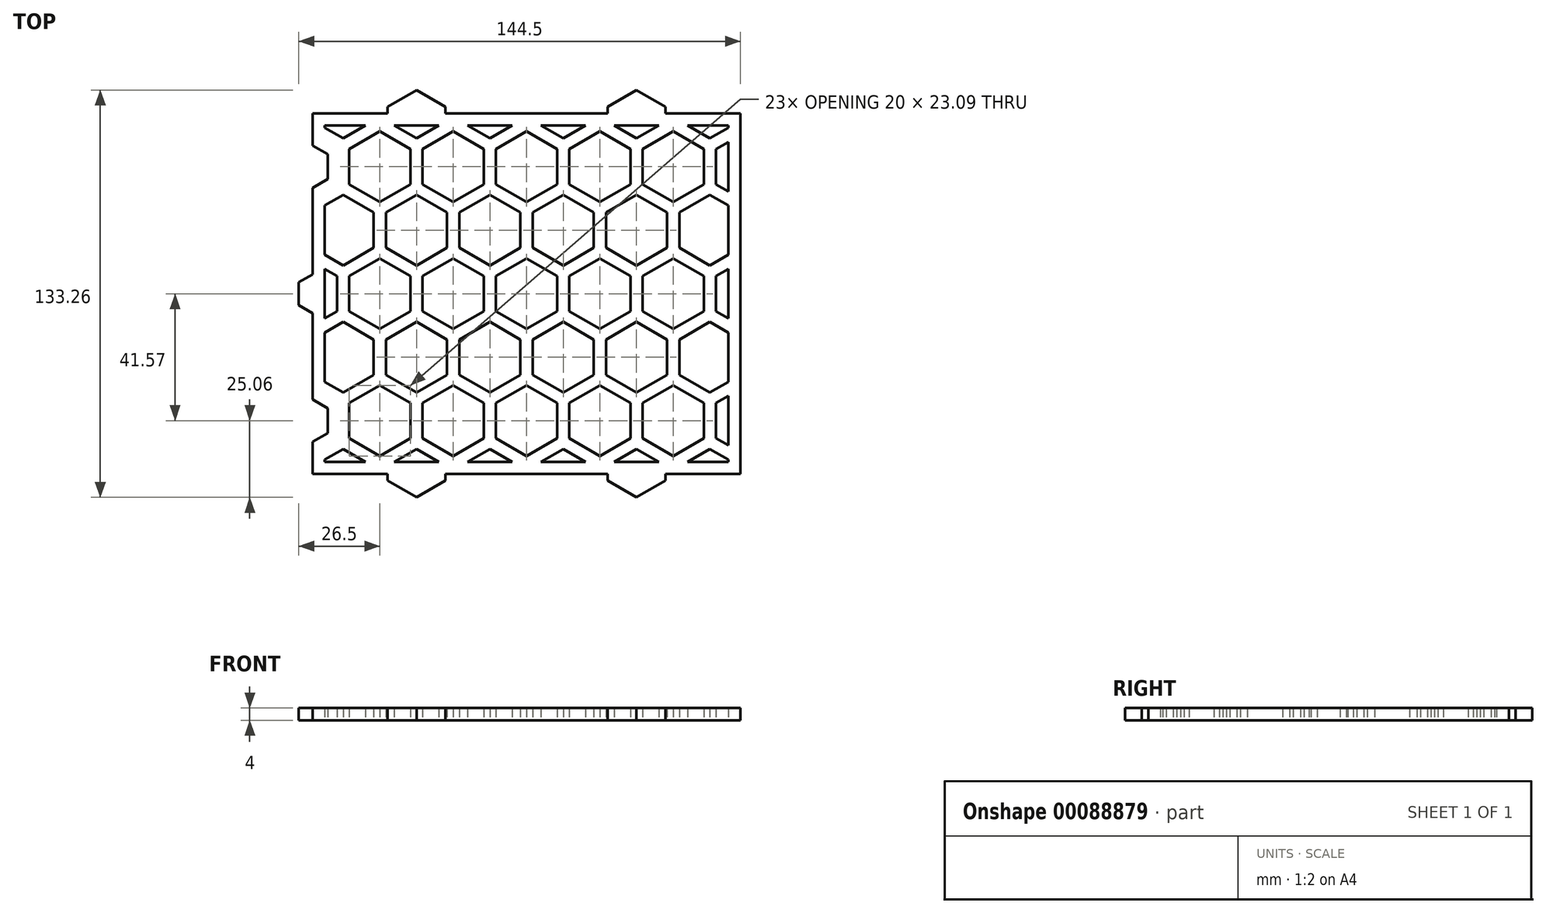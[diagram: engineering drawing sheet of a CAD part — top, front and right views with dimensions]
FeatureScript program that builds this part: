
annotation { "Feature Type Name" : "Feature", "Feature Type Description" : "" }
export const myFeature = defineFeature(function(context is Context, id is Id, definition is map)
    precondition{}
    {
        {
            var Q0;
            Q0=qCreatedBy(makeId("Top.planeOp"),FACE);
            var sketch = newSketch(context, id + "F0", { "sketchPlane" : qUnion([Q0])});
            skLineSegment(sketch, "E0.bottom", {"start": v(70, -59) * mm, "end": v(-70, -59) * mm});
            skLineSegment(sketch, "E0.top", {"start": v(70, 59) * mm, "end": v(-70, 59) * mm});
            skLineSegment(sketch, "E0.left", {"start": v(70, -59) * mm, "end": v(70, 59) * mm});
            skLineSegment(sketch, "E0.right", {"start": v(-70, -59) * mm, "end": v(-70, 59) * mm});
            skPoint(sketch, "E0.middle", {"position": v(0, 0) * mm});
            skLineSegment(sketch, "E1.0", {"start": v(-66, -55) * mm, "end": v(-66, 55) * mm});
            skLineSegment(sketch, "E1.1", {"start": v(66, -55) * mm, "end": v(-66, -55) * mm});
            skLineSegment(sketch, "E1.2", {"start": v(66, -55) * mm, "end": v(66, 55) * mm});
            skLineSegment(sketch, "E1.3", {"start": v(66, 55) * mm, "end": v(-66, 55) * mm});
            skSolve(sketch);
        }
        {
            var Q0;
            Q0=qSketchRegion(id+"F0",true);
            extrude(context, id + "F1", {"entities" : qUnion([Q0]), "depth" : 4 * mm});
        }
        {
            var Q0;
            Q0=qCreatedBy(makeId("Top.planeOp"),FACE);
            var sketch = newSketch(context, id + "F2", { "sketchPlane" : qUnion([Q0])});
            skLineSegment(sketch, "E2.0.1.1", {"start": v(-62, -47.34) * mm, "end": v(-66, -49.65) * mm});
            skLineSegment(sketch, "E2.0.1.5", {"start": v(-66, -33.49) * mm, "end": v(-62, -35.8) * mm});
            skLineSegment(sketch, "E2.0.1.13", {"start": v(-62, -35.8) * mm, "end": v(-62, -47.34) * mm});
            skLineSegment(sketch, "E2.0.2.1", {"start": v(-62, -5.77) * mm, "end": v(-66, -8.08) * mm});
            skLineSegment(sketch, "E2.0.2.5", {"start": v(-66, 8.08) * mm, "end": v(-62, 5.77) * mm});
            skLineSegment(sketch, "E2.0.2.13", {"start": v(-62, 5.77) * mm, "end": v(-62, -5.77) * mm});
            skLineSegment(sketch, "E2.0.3.1", {"start": v(-62, 35.8) * mm, "end": v(-66, 33.49) * mm});
            skLineSegment(sketch, "E2.0.3.5", {"start": v(-66, 49.65) * mm, "end": v(-62, 47.34) * mm});
            skLineSegment(sketch, "E2.0.3.13", {"start": v(-62, 47.34) * mm, "end": v(-62, 35.8) * mm});
            skLineSegment(sketch, "E2.1.0.7", {"start": v(-60, -50.8) * mm, "end": v(-52.74, -55) * mm});
            skLineSegment(sketch, "E2.1.0.8", {"start": v(-66, -54.27) * mm, "end": v(-60, -50.8) * mm});
            skCircle(sketch, "E2.1.1.0", {"center": v(-48, -41.57) * mm, "radius": 11.55 * mm, "construction": true});
            skLineSegment(sketch, "E2.1.1.1", {"start": v(-38, -47.34) * mm, "end": v(-48, -53.12) * mm});
            skLineSegment(sketch, "E2.1.1.2", {"start": v(-48, -53.12) * mm, "end": v(-58, -47.34) * mm});
            skLineSegment(sketch, "E2.1.1.3", {"start": v(-58, -47.34) * mm, "end": v(-58, -35.8) * mm});
            skLineSegment(sketch, "E2.1.1.4", {"start": v(-58, -35.8) * mm, "end": v(-48, -30.02) * mm});
            skLineSegment(sketch, "E2.1.1.5", {"start": v(-48, -30.02) * mm, "end": v(-38, -35.8) * mm});
            skLineSegment(sketch, "E2.1.1.6", {"start": v(-50, -15.01) * mm, "end": v(-50, -26.56) * mm});
            skLineSegment(sketch, "E2.1.1.7", {"start": v(-60, -9.24) * mm, "end": v(-50, -15.01) * mm});
            skLineSegment(sketch, "E2.1.1.8", {"start": v(-66, -12.7) * mm, "end": v(-60, -9.24) * mm});
            skLineSegment(sketch, "E2.1.1.10", {"start": v(-60, -32.33) * mm, "end": v(-66, -28.87) * mm});
            skLineSegment(sketch, "E2.1.1.11", {"start": v(-50, -26.56) * mm, "end": v(-60, -32.33) * mm});
            skLineSegment(sketch, "E2.1.1.13", {"start": v(-38, -35.8) * mm, "end": v(-38, -47.34) * mm});
            skCircle(sketch, "E2.1.2.0", {"center": v(-48, 0) * mm, "radius": 11.55 * mm, "construction": true});
            skLineSegment(sketch, "E2.1.2.1", {"start": v(-38, -5.77) * mm, "end": v(-48, -11.55) * mm});
            skLineSegment(sketch, "E2.1.2.2", {"start": v(-48, -11.55) * mm, "end": v(-58, -5.77) * mm});
            skLineSegment(sketch, "E2.1.2.3", {"start": v(-58, -5.77) * mm, "end": v(-58, 5.77) * mm});
            skLineSegment(sketch, "E2.1.2.4", {"start": v(-58, 5.77) * mm, "end": v(-48, 11.55) * mm});
            skLineSegment(sketch, "E2.1.2.5", {"start": v(-48, 11.55) * mm, "end": v(-38, 5.77) * mm});
            skLineSegment(sketch, "E2.1.2.6", {"start": v(-50, 26.56) * mm, "end": v(-50, 15.01) * mm});
            skLineSegment(sketch, "E2.1.2.7", {"start": v(-60, 32.33) * mm, "end": v(-50, 26.56) * mm});
            skLineSegment(sketch, "E2.1.2.8", {"start": v(-66, 28.87) * mm, "end": v(-60, 32.33) * mm});
            skLineSegment(sketch, "E2.1.2.10", {"start": v(-60, 9.24) * mm, "end": v(-66, 12.7) * mm});
            skLineSegment(sketch, "E2.1.2.11", {"start": v(-50, 15.01) * mm, "end": v(-60, 9.24) * mm});
            skLineSegment(sketch, "E2.1.2.13", {"start": v(-38, 5.77) * mm, "end": v(-38, -5.77) * mm});
            skCircle(sketch, "E2.1.3.0", {"center": v(-48, 41.57) * mm, "radius": 11.55 * mm, "construction": true});
            skLineSegment(sketch, "E2.1.3.1", {"start": v(-38, 35.8) * mm, "end": v(-48, 30.02) * mm});
            skLineSegment(sketch, "E2.1.3.2", {"start": v(-48, 30.02) * mm, "end": v(-58, 35.8) * mm});
            skLineSegment(sketch, "E2.1.3.3", {"start": v(-58, 35.8) * mm, "end": v(-58, 47.34) * mm});
            skLineSegment(sketch, "E2.1.3.4", {"start": v(-58, 47.34) * mm, "end": v(-48, 53.12) * mm});
            skLineSegment(sketch, "E2.1.3.5", {"start": v(-48, 53.12) * mm, "end": v(-38, 47.34) * mm});
            skLineSegment(sketch, "E2.1.3.10", {"start": v(-60, 50.8) * mm, "end": v(-66, 54.27) * mm});
            skLineSegment(sketch, "E2.1.3.11", {"start": v(-52.74, 55) * mm, "end": v(-60, 50.8) * mm});
            skLineSegment(sketch, "E2.1.3.13", {"start": v(-38, 47.34) * mm, "end": v(-38, 35.8) * mm});
            skLineSegment(sketch, "E2.2.0.7", {"start": v(-36, -50.8) * mm, "end": v(-28.74, -55) * mm});
            skLineSegment(sketch, "E2.2.0.8", {"start": v(-43.26, -55) * mm, "end": v(-36, -50.8) * mm});
            skCircle(sketch, "E2.2.1.0", {"center": v(-24, -41.57) * mm, "radius": 11.55 * mm, "construction": true});
            skLineSegment(sketch, "E2.2.1.1", {"start": v(-14, -47.34) * mm, "end": v(-24, -53.12) * mm});
            skLineSegment(sketch, "E2.2.1.2", {"start": v(-24, -53.12) * mm, "end": v(-34, -47.34) * mm});
            skLineSegment(sketch, "E2.2.1.3", {"start": v(-34, -47.34) * mm, "end": v(-34, -35.8) * mm});
            skLineSegment(sketch, "E2.2.1.4", {"start": v(-34, -35.8) * mm, "end": v(-24, -30.02) * mm});
            skLineSegment(sketch, "E2.2.1.5", {"start": v(-24, -30.02) * mm, "end": v(-14, -35.8) * mm});
            skLineSegment(sketch, "E2.2.1.6", {"start": v(-26, -15.01) * mm, "end": v(-26, -26.56) * mm});
            skLineSegment(sketch, "E2.2.1.7", {"start": v(-36, -9.24) * mm, "end": v(-26, -15.01) * mm});
            skLineSegment(sketch, "E2.2.1.8", {"start": v(-46, -15.01) * mm, "end": v(-36, -9.24) * mm});
            skLineSegment(sketch, "E2.2.1.9", {"start": v(-46, -26.56) * mm, "end": v(-46, -15.01) * mm});
            skLineSegment(sketch, "E2.2.1.10", {"start": v(-36, -32.33) * mm, "end": v(-46, -26.56) * mm});
            skLineSegment(sketch, "E2.2.1.11", {"start": v(-26, -26.56) * mm, "end": v(-36, -32.33) * mm});
            skCircle(sketch, "E2.2.1.12", {"center": v(-36, -20.79) * mm, "radius": 11.55 * mm, "construction": true});
            skLineSegment(sketch, "E2.2.1.13", {"start": v(-14, -35.8) * mm, "end": v(-14, -47.34) * mm});
            skCircle(sketch, "E2.2.2.0", {"center": v(-24, 0) * mm, "radius": 11.55 * mm, "construction": true});
            skLineSegment(sketch, "E2.2.2.1", {"start": v(-14, -5.77) * mm, "end": v(-24, -11.55) * mm});
            skLineSegment(sketch, "E2.2.2.2", {"start": v(-24, -11.55) * mm, "end": v(-34, -5.77) * mm});
            skLineSegment(sketch, "E2.2.2.3", {"start": v(-34, -5.77) * mm, "end": v(-34, 5.77) * mm});
            skLineSegment(sketch, "E2.2.2.4", {"start": v(-34, 5.77) * mm, "end": v(-24, 11.55) * mm});
            skLineSegment(sketch, "E2.2.2.5", {"start": v(-24, 11.55) * mm, "end": v(-14, 5.77) * mm});
            skLineSegment(sketch, "E2.2.2.6", {"start": v(-26, 26.56) * mm, "end": v(-26, 15.01) * mm});
            skLineSegment(sketch, "E2.2.2.7", {"start": v(-36, 32.33) * mm, "end": v(-26, 26.56) * mm});
            skLineSegment(sketch, "E2.2.2.8", {"start": v(-46, 26.56) * mm, "end": v(-36, 32.33) * mm});
            skLineSegment(sketch, "E2.2.2.9", {"start": v(-46, 15.01) * mm, "end": v(-46, 26.56) * mm});
            skLineSegment(sketch, "E2.2.2.10", {"start": v(-36, 9.24) * mm, "end": v(-46, 15.01) * mm});
            skLineSegment(sketch, "E2.2.2.11", {"start": v(-26, 15.01) * mm, "end": v(-36, 9.24) * mm});
            skCircle(sketch, "E2.2.2.12", {"center": v(-36, 20.78) * mm, "radius": 11.55 * mm, "construction": true});
            skLineSegment(sketch, "E2.2.2.13", {"start": v(-14, 5.77) * mm, "end": v(-14, -5.77) * mm});
            skCircle(sketch, "E2.2.3.0", {"center": v(-24, 41.57) * mm, "radius": 11.55 * mm, "construction": true});
            skLineSegment(sketch, "E2.2.3.1", {"start": v(-14, 35.8) * mm, "end": v(-24, 30.02) * mm});
            skLineSegment(sketch, "E2.2.3.2", {"start": v(-24, 30.02) * mm, "end": v(-34, 35.8) * mm});
            skLineSegment(sketch, "E2.2.3.3", {"start": v(-34, 35.8) * mm, "end": v(-34, 47.34) * mm});
            skLineSegment(sketch, "E2.2.3.4", {"start": v(-34, 47.34) * mm, "end": v(-24, 53.12) * mm});
            skLineSegment(sketch, "E2.2.3.5", {"start": v(-24, 53.12) * mm, "end": v(-14, 47.34) * mm});
            skLineSegment(sketch, "E2.2.3.10", {"start": v(-36, 50.8) * mm, "end": v(-43.26, 55) * mm});
            skLineSegment(sketch, "E2.2.3.11", {"start": v(-28.74, 55) * mm, "end": v(-36, 50.8) * mm});
            skLineSegment(sketch, "E2.2.3.13", {"start": v(-14, 47.34) * mm, "end": v(-14, 35.8) * mm});
            skLineSegment(sketch, "E2.3.0.7", {"start": v(-12, -50.8) * mm, "end": v(-4.74, -55) * mm});
            skLineSegment(sketch, "E2.3.0.8", {"start": v(-19.26, -55) * mm, "end": v(-12, -50.8) * mm});
            skCircle(sketch, "E2.3.1.0", {"center": v(0, -41.57) * mm, "radius": 11.55 * mm, "construction": true});
            skLineSegment(sketch, "E2.3.1.1", {"start": v(10, -47.34) * mm, "end": v(0, -53.12) * mm});
            skLineSegment(sketch, "E2.3.1.2", {"start": v(0, -53.12) * mm, "end": v(-10, -47.34) * mm});
            skLineSegment(sketch, "E2.3.1.3", {"start": v(-10, -47.34) * mm, "end": v(-10, -35.8) * mm});
            skLineSegment(sketch, "E2.3.1.4", {"start": v(-10, -35.8) * mm, "end": v(0, -30.02) * mm});
            skLineSegment(sketch, "E2.3.1.5", {"start": v(0, -30.02) * mm, "end": v(10, -35.8) * mm});
            skLineSegment(sketch, "E2.3.1.6", {"start": v(-2, -15.01) * mm, "end": v(-2, -26.56) * mm});
            skLineSegment(sketch, "E2.3.1.7", {"start": v(-12, -9.24) * mm, "end": v(-2, -15.01) * mm});
            skLineSegment(sketch, "E2.3.1.8", {"start": v(-22, -15.01) * mm, "end": v(-12, -9.24) * mm});
            skLineSegment(sketch, "E2.3.1.9", {"start": v(-22, -26.56) * mm, "end": v(-22, -15.01) * mm});
            skLineSegment(sketch, "E2.3.1.10", {"start": v(-12, -32.33) * mm, "end": v(-22, -26.56) * mm});
            skLineSegment(sketch, "E2.3.1.11", {"start": v(-2, -26.56) * mm, "end": v(-12, -32.33) * mm});
            skCircle(sketch, "E2.3.1.12", {"center": v(-12, -20.79) * mm, "radius": 11.55 * mm, "construction": true});
            skLineSegment(sketch, "E2.3.1.13", {"start": v(10, -35.8) * mm, "end": v(10, -47.34) * mm});
            skCircle(sketch, "E2.3.2.0", {"center": v(0, 0) * mm, "radius": 11.55 * mm, "construction": true});
            skLineSegment(sketch, "E2.3.2.1", {"start": v(10, -5.77) * mm, "end": v(0, -11.55) * mm});
            skLineSegment(sketch, "E2.3.2.2", {"start": v(0, -11.55) * mm, "end": v(-10, -5.77) * mm});
            skLineSegment(sketch, "E2.3.2.3", {"start": v(-10, -5.77) * mm, "end": v(-10, 5.77) * mm});
            skLineSegment(sketch, "E2.3.2.4", {"start": v(-10, 5.77) * mm, "end": v(0, 11.55) * mm});
            skLineSegment(sketch, "E2.3.2.5", {"start": v(0, 11.55) * mm, "end": v(10, 5.77) * mm});
            skLineSegment(sketch, "E2.3.2.6", {"start": v(-2, 26.56) * mm, "end": v(-2, 15.01) * mm});
            skLineSegment(sketch, "E2.3.2.7", {"start": v(-12, 32.33) * mm, "end": v(-2, 26.56) * mm});
            skLineSegment(sketch, "E2.3.2.8", {"start": v(-22, 26.56) * mm, "end": v(-12, 32.33) * mm});
            skLineSegment(sketch, "E2.3.2.9", {"start": v(-22, 15.01) * mm, "end": v(-22, 26.56) * mm});
            skLineSegment(sketch, "E2.3.2.10", {"start": v(-12, 9.24) * mm, "end": v(-22, 15.01) * mm});
            skLineSegment(sketch, "E2.3.2.11", {"start": v(-2, 15.01) * mm, "end": v(-12, 9.24) * mm});
            skCircle(sketch, "E2.3.2.12", {"center": v(-12, 20.78) * mm, "radius": 11.55 * mm, "construction": true});
            skLineSegment(sketch, "E2.3.2.13", {"start": v(10, 5.77) * mm, "end": v(10, -5.77) * mm});
            skCircle(sketch, "E2.3.3.0", {"center": v(0, 41.57) * mm, "radius": 11.55 * mm, "construction": true});
            skLineSegment(sketch, "E2.3.3.1", {"start": v(10, 35.8) * mm, "end": v(0, 30.02) * mm});
            skLineSegment(sketch, "E2.3.3.2", {"start": v(0, 30.02) * mm, "end": v(-10, 35.8) * mm});
            skLineSegment(sketch, "E2.3.3.3", {"start": v(-10, 35.8) * mm, "end": v(-10, 47.34) * mm});
            skLineSegment(sketch, "E2.3.3.4", {"start": v(-10, 47.34) * mm, "end": v(0, 53.12) * mm});
            skLineSegment(sketch, "E2.3.3.5", {"start": v(0, 53.12) * mm, "end": v(10, 47.34) * mm});
            skLineSegment(sketch, "E2.3.3.10", {"start": v(-12, 50.8) * mm, "end": v(-19.26, 55) * mm});
            skLineSegment(sketch, "E2.3.3.11", {"start": v(-4.74, 55) * mm, "end": v(-12, 50.8) * mm});
            skLineSegment(sketch, "E2.3.3.13", {"start": v(10, 47.34) * mm, "end": v(10, 35.8) * mm});
            skLineSegment(sketch, "E2.4.0.7", {"start": v(12, -50.8) * mm, "end": v(19.26, -55) * mm});
            skLineSegment(sketch, "E2.4.0.8", {"start": v(4.74, -55) * mm, "end": v(12, -50.8) * mm});
            skCircle(sketch, "E2.4.1.0", {"center": v(24, -41.57) * mm, "radius": 11.55 * mm, "construction": true});
            skLineSegment(sketch, "E2.4.1.1", {"start": v(34, -47.34) * mm, "end": v(24, -53.12) * mm});
            skLineSegment(sketch, "E2.4.1.2", {"start": v(24, -53.12) * mm, "end": v(14, -47.34) * mm});
            skLineSegment(sketch, "E2.4.1.3", {"start": v(14, -47.34) * mm, "end": v(14, -35.8) * mm});
            skLineSegment(sketch, "E2.4.1.4", {"start": v(14, -35.8) * mm, "end": v(24, -30.02) * mm});
            skLineSegment(sketch, "E2.4.1.5", {"start": v(24, -30.02) * mm, "end": v(34, -35.8) * mm});
            skLineSegment(sketch, "E2.4.1.6", {"start": v(22, -15.01) * mm, "end": v(22, -26.56) * mm});
            skLineSegment(sketch, "E2.4.1.7", {"start": v(12, -9.24) * mm, "end": v(22, -15.01) * mm});
            skLineSegment(sketch, "E2.4.1.8", {"start": v(2, -15.01) * mm, "end": v(12, -9.24) * mm});
            skLineSegment(sketch, "E2.4.1.9", {"start": v(2, -26.56) * mm, "end": v(2, -15.01) * mm});
            skLineSegment(sketch, "E2.4.1.10", {"start": v(12, -32.33) * mm, "end": v(2, -26.56) * mm});
            skLineSegment(sketch, "E2.4.1.11", {"start": v(22, -26.56) * mm, "end": v(12, -32.33) * mm});
            skCircle(sketch, "E2.4.1.12", {"center": v(12, -20.79) * mm, "radius": 11.55 * mm, "construction": true});
            skLineSegment(sketch, "E2.4.1.13", {"start": v(34, -35.8) * mm, "end": v(34, -47.34) * mm});
            skCircle(sketch, "E2.4.2.0", {"center": v(24, 0) * mm, "radius": 11.55 * mm, "construction": true});
            skLineSegment(sketch, "E2.4.2.1", {"start": v(34, -5.77) * mm, "end": v(24, -11.55) * mm});
            skLineSegment(sketch, "E2.4.2.2", {"start": v(24, -11.55) * mm, "end": v(14, -5.77) * mm});
            skLineSegment(sketch, "E2.4.2.3", {"start": v(14, -5.77) * mm, "end": v(14, 5.77) * mm});
            skLineSegment(sketch, "E2.4.2.4", {"start": v(14, 5.77) * mm, "end": v(24, 11.55) * mm});
            skLineSegment(sketch, "E2.4.2.5", {"start": v(24, 11.55) * mm, "end": v(34, 5.77) * mm});
            skLineSegment(sketch, "E2.4.2.6", {"start": v(22, 26.56) * mm, "end": v(22, 15.01) * mm});
            skLineSegment(sketch, "E2.4.2.7", {"start": v(12, 32.33) * mm, "end": v(22, 26.56) * mm});
            skLineSegment(sketch, "E2.4.2.8", {"start": v(2, 26.56) * mm, "end": v(12, 32.33) * mm});
            skLineSegment(sketch, "E2.4.2.9", {"start": v(2, 15.01) * mm, "end": v(2, 26.56) * mm});
            skLineSegment(sketch, "E2.4.2.10", {"start": v(12, 9.24) * mm, "end": v(2, 15.01) * mm});
            skLineSegment(sketch, "E2.4.2.11", {"start": v(22, 15.01) * mm, "end": v(12, 9.24) * mm});
            skCircle(sketch, "E2.4.2.12", {"center": v(12, 20.78) * mm, "radius": 11.55 * mm, "construction": true});
            skLineSegment(sketch, "E2.4.2.13", {"start": v(34, 5.77) * mm, "end": v(34, -5.77) * mm});
            skCircle(sketch, "E2.4.3.0", {"center": v(24, 41.57) * mm, "radius": 11.55 * mm, "construction": true});
            skLineSegment(sketch, "E2.4.3.1", {"start": v(34, 35.8) * mm, "end": v(24, 30.02) * mm});
            skLineSegment(sketch, "E2.4.3.2", {"start": v(24, 30.02) * mm, "end": v(14, 35.8) * mm});
            skLineSegment(sketch, "E2.4.3.3", {"start": v(14, 35.8) * mm, "end": v(14, 47.34) * mm});
            skLineSegment(sketch, "E2.4.3.4", {"start": v(14, 47.34) * mm, "end": v(24, 53.12) * mm});
            skLineSegment(sketch, "E2.4.3.5", {"start": v(24, 53.12) * mm, "end": v(34, 47.34) * mm});
            skLineSegment(sketch, "E2.4.3.10", {"start": v(12, 50.8) * mm, "end": v(4.74, 55) * mm});
            skLineSegment(sketch, "E2.4.3.11", {"start": v(19.26, 55) * mm, "end": v(12, 50.8) * mm});
            skLineSegment(sketch, "E2.4.3.13", {"start": v(34, 47.34) * mm, "end": v(34, 35.8) * mm});
            skLineSegment(sketch, "E2.5.0.7", {"start": v(36, -50.8) * mm, "end": v(43.26, -55) * mm});
            skLineSegment(sketch, "E2.5.0.8", {"start": v(28.74, -55) * mm, "end": v(36, -50.8) * mm});
            skCircle(sketch, "E2.5.1.0", {"center": v(48, -41.57) * mm, "radius": 11.55 * mm, "construction": true});
            skLineSegment(sketch, "E2.5.1.1", {"start": v(58, -47.34) * mm, "end": v(48, -53.12) * mm});
            skLineSegment(sketch, "E2.5.1.2", {"start": v(48, -53.12) * mm, "end": v(38, -47.34) * mm});
            skLineSegment(sketch, "E2.5.1.3", {"start": v(38, -47.34) * mm, "end": v(38, -35.8) * mm});
            skLineSegment(sketch, "E2.5.1.4", {"start": v(38, -35.8) * mm, "end": v(48, -30.02) * mm});
            skLineSegment(sketch, "E2.5.1.5", {"start": v(48, -30.02) * mm, "end": v(58, -35.8) * mm});
            skLineSegment(sketch, "E2.5.1.6", {"start": v(46, -15.01) * mm, "end": v(46, -26.56) * mm});
            skLineSegment(sketch, "E2.5.1.7", {"start": v(36, -9.24) * mm, "end": v(46, -15.01) * mm});
            skLineSegment(sketch, "E2.5.1.8", {"start": v(26, -15.01) * mm, "end": v(36, -9.24) * mm});
            skLineSegment(sketch, "E2.5.1.9", {"start": v(26, -26.56) * mm, "end": v(26, -15.01) * mm});
            skLineSegment(sketch, "E2.5.1.10", {"start": v(36, -32.33) * mm, "end": v(26, -26.56) * mm});
            skLineSegment(sketch, "E2.5.1.11", {"start": v(46, -26.56) * mm, "end": v(36, -32.33) * mm});
            skCircle(sketch, "E2.5.1.12", {"center": v(36, -20.79) * mm, "radius": 11.55 * mm, "construction": true});
            skLineSegment(sketch, "E2.5.1.13", {"start": v(58, -35.8) * mm, "end": v(58, -47.34) * mm});
            skCircle(sketch, "E2.5.2.0", {"center": v(48, 0) * mm, "radius": 11.55 * mm, "construction": true});
            skLineSegment(sketch, "E2.5.2.1", {"start": v(58, -5.77) * mm, "end": v(48, -11.55) * mm});
            skLineSegment(sketch, "E2.5.2.2", {"start": v(48, -11.55) * mm, "end": v(38, -5.77) * mm});
            skLineSegment(sketch, "E2.5.2.3", {"start": v(38, -5.77) * mm, "end": v(38, 5.77) * mm});
            skLineSegment(sketch, "E2.5.2.4", {"start": v(38, 5.77) * mm, "end": v(48, 11.55) * mm});
            skLineSegment(sketch, "E2.5.2.5", {"start": v(48, 11.55) * mm, "end": v(58, 5.77) * mm});
            skLineSegment(sketch, "E2.5.2.6", {"start": v(46, 26.56) * mm, "end": v(46, 15.01) * mm});
            skLineSegment(sketch, "E2.5.2.7", {"start": v(36, 32.33) * mm, "end": v(46, 26.56) * mm});
            skLineSegment(sketch, "E2.5.2.8", {"start": v(26, 26.56) * mm, "end": v(36, 32.33) * mm});
            skLineSegment(sketch, "E2.5.2.9", {"start": v(26, 15.01) * mm, "end": v(26, 26.56) * mm});
            skLineSegment(sketch, "E2.5.2.10", {"start": v(36, 9.24) * mm, "end": v(26, 15.01) * mm});
            skLineSegment(sketch, "E2.5.2.11", {"start": v(46, 15.01) * mm, "end": v(36, 9.24) * mm});
            skCircle(sketch, "E2.5.2.12", {"center": v(36, 20.78) * mm, "radius": 11.55 * mm, "construction": true});
            skLineSegment(sketch, "E2.5.2.13", {"start": v(58, 5.77) * mm, "end": v(58, -5.77) * mm});
            skCircle(sketch, "E2.5.3.0", {"center": v(48, 41.57) * mm, "radius": 11.55 * mm, "construction": true});
            skLineSegment(sketch, "E2.5.3.1", {"start": v(58, 35.8) * mm, "end": v(48, 30.02) * mm});
            skLineSegment(sketch, "E2.5.3.2", {"start": v(48, 30.02) * mm, "end": v(38, 35.8) * mm});
            skLineSegment(sketch, "E2.5.3.3", {"start": v(38, 35.8) * mm, "end": v(38, 47.34) * mm});
            skLineSegment(sketch, "E2.5.3.4", {"start": v(38, 47.34) * mm, "end": v(48, 53.12) * mm});
            skLineSegment(sketch, "E2.5.3.5", {"start": v(48, 53.12) * mm, "end": v(58, 47.34) * mm});
            skLineSegment(sketch, "E2.5.3.10", {"start": v(36, 50.8) * mm, "end": v(28.74, 55) * mm});
            skLineSegment(sketch, "E2.5.3.11", {"start": v(43.26, 55) * mm, "end": v(36, 50.8) * mm});
            skLineSegment(sketch, "E2.5.3.13", {"start": v(58, 47.34) * mm, "end": v(58, 35.8) * mm});
            skLineSegment(sketch, "E2.6.0.7", {"start": v(60, -50.8) * mm, "end": v(66, -54.27) * mm});
            skLineSegment(sketch, "E2.6.0.8", {"start": v(52.74, -55) * mm, "end": v(60, -50.8) * mm});
            skLineSegment(sketch, "E2.6.1.2", {"start": v(66, -49.65) * mm, "end": v(62, -47.34) * mm});
            skLineSegment(sketch, "E2.6.1.3", {"start": v(62, -47.34) * mm, "end": v(62, -35.8) * mm});
            skLineSegment(sketch, "E2.6.1.4", {"start": v(62, -35.8) * mm, "end": v(66, -33.49) * mm});
            skLineSegment(sketch, "E2.6.1.7", {"start": v(60, -9.24) * mm, "end": v(66, -12.7) * mm});
            skLineSegment(sketch, "E2.6.1.8", {"start": v(50, -15.01) * mm, "end": v(60, -9.24) * mm});
            skLineSegment(sketch, "E2.6.1.9", {"start": v(50, -26.56) * mm, "end": v(50, -15.01) * mm});
            skLineSegment(sketch, "E2.6.1.10", {"start": v(60, -32.33) * mm, "end": v(50, -26.56) * mm});
            skLineSegment(sketch, "E2.6.1.11", {"start": v(66, -28.87) * mm, "end": v(60, -32.33) * mm});
            skLineSegment(sketch, "E2.6.2.2", {"start": v(66, -8.08) * mm, "end": v(62, -5.77) * mm});
            skLineSegment(sketch, "E2.6.2.3", {"start": v(62, -5.77) * mm, "end": v(62, 5.77) * mm});
            skLineSegment(sketch, "E2.6.2.4", {"start": v(62, 5.77) * mm, "end": v(66, 8.08) * mm});
            skLineSegment(sketch, "E2.6.2.7", {"start": v(60, 32.33) * mm, "end": v(66, 28.87) * mm});
            skLineSegment(sketch, "E2.6.2.8", {"start": v(50, 26.56) * mm, "end": v(60, 32.33) * mm});
            skLineSegment(sketch, "E2.6.2.9", {"start": v(50, 15.01) * mm, "end": v(50, 26.56) * mm});
            skLineSegment(sketch, "E2.6.2.10", {"start": v(60, 9.24) * mm, "end": v(50, 15.01) * mm});
            skLineSegment(sketch, "E2.6.2.11", {"start": v(66, 12.7) * mm, "end": v(60, 9.24) * mm});
            skLineSegment(sketch, "E2.6.3.2", {"start": v(66, 33.49) * mm, "end": v(62, 35.8) * mm});
            skLineSegment(sketch, "E2.6.3.3", {"start": v(62, 35.8) * mm, "end": v(62, 47.34) * mm});
            skLineSegment(sketch, "E2.6.3.4", {"start": v(62, 47.34) * mm, "end": v(66, 49.65) * mm});
            skLineSegment(sketch, "E2.6.3.10", {"start": v(60, 50.8) * mm, "end": v(52.74, 55) * mm});
            skLineSegment(sketch, "E2.6.3.11", {"start": v(66, 54.27) * mm, "end": v(60, 50.8) * mm});
            skLineSegment(sketch, "E3.0", {"start": v(-66, -55) * mm, "end": v(-66, -54.27) * mm});
            skLineSegment(sketch, "E3.1", {"start": v(66, 55) * mm, "end": v(52.74, 55) * mm});
            skLineSegment(sketch, "E3.2", {"start": v(66, -55) * mm, "end": v(66, -54.27) * mm});
            skLineSegment(sketch, "E3.3", {"start": v(66, -55) * mm, "end": v(52.74, -55) * mm});
            skLineSegment(sketch, "E4.trimOffspring", {"start": v(-66, 54.27) * mm, "end": v(-66, 55) * mm});
            skLineSegment(sketch, "E5.trimOffspring", {"start": v(-66, 33.49) * mm, "end": v(-66, 49.65) * mm});
            skLineSegment(sketch, "E6.trimOffspring", {"start": v(-66, 12.7) * mm, "end": v(-66, 28.87) * mm});
            skLineSegment(sketch, "E7.trimOffspring", {"start": v(-52.74, 55) * mm, "end": v(-66, 55) * mm});
            skLineSegment(sketch, "E8.trimOffspring", {"start": v(-28.74, 55) * mm, "end": v(-43.26, 55) * mm});
            skLineSegment(sketch, "E9.trimOffspring", {"start": v(-4.74, 55) * mm, "end": v(-19.26, 55) * mm});
            skLineSegment(sketch, "E10.trimOffspring", {"start": v(19.26, 55) * mm, "end": v(4.74, 55) * mm});
            skLineSegment(sketch, "E11.trimOffspring", {"start": v(43.26, 55) * mm, "end": v(28.74, 55) * mm});
            skLineSegment(sketch, "E12.trimOffspring", {"start": v(66, 54.27) * mm, "end": v(66, 55) * mm});
            skLineSegment(sketch, "E13.trimOffspring", {"start": v(66, 33.49) * mm, "end": v(66, 49.65) * mm});
            skLineSegment(sketch, "E14.trimOffspring", {"start": v(66, 12.7) * mm, "end": v(66, 28.87) * mm});
            skLineSegment(sketch, "E15.trimOffspring", {"start": v(66, -8.08) * mm, "end": v(66, 8.08) * mm});
            skLineSegment(sketch, "E16.trimOffspring", {"start": v(66, -28.87) * mm, "end": v(66, -12.7) * mm});
            skLineSegment(sketch, "E17.trimOffspring", {"start": v(66, -49.65) * mm, "end": v(66, -33.49) * mm});
            skLineSegment(sketch, "E18.trimOffspring", {"start": v(43.26, -55) * mm, "end": v(28.74, -55) * mm});
            skLineSegment(sketch, "E19.trimOffspring", {"start": v(19.26, -55) * mm, "end": v(4.74, -55) * mm});
            skLineSegment(sketch, "E20.trimOffspring", {"start": v(-4.74, -55) * mm, "end": v(-19.26, -55) * mm});
            skLineSegment(sketch, "E21.trimOffspring", {"start": v(-28.74, -55) * mm, "end": v(-43.26, -55) * mm});
            skLineSegment(sketch, "E22.trimOffspring", {"start": v(-52.74, -55) * mm, "end": v(-66, -55) * mm});
            skLineSegment(sketch, "E23.trimOffspring", {"start": v(-66, -49.65) * mm, "end": v(-66, -33.49) * mm});
            skLineSegment(sketch, "E24.trimOffspring", {"start": v(-66, -28.87) * mm, "end": v(-66, -12.7) * mm});
            skLineSegment(sketch, "E25.trimOffspring", {"start": v(-66, -8.08) * mm, "end": v(-66, 8.08) * mm});
            skLineSegment(sketch, "E26.0", {"start": v(-70, -59) * mm, "end": v(-70, 59) * mm});
            skLineSegment(sketch, "E26.1", {"start": v(70, 59) * mm, "end": v(-70, 59) * mm});
            skLineSegment(sketch, "E26.2", {"start": v(70, -59) * mm, "end": v(70, 59) * mm});
            skLineSegment(sketch, "E26.3", {"start": v(70, -59) * mm, "end": v(-70, -59) * mm});
            skSolve(sketch);
        }
        {
            var Q0;
            Q0=qSketchRegion(id+"F2",true);
            var Q1;
            Q1=makeQuery(id+"F1.opExtrude","CAP_FACE",FACE,{"disambiguationData":[OSD([sQuery(id+"F0.wireOp",EDGE,"E0.bottom"),sQuery(id+"F0.wireOp",EDGE,"E0.top"),sQuery(id+"F0.wireOp",EDGE,"E0.left"),sQuery(id+"F0.wireOp",EDGE,"E0.right"),sQuery(id+"F0.wireOp",EDGE,"E1.0"),sQuery(id+"F0.wireOp",EDGE,"E1.1"),sQuery(id+"F0.wireOp",EDGE,"E1.2"),sQuery(id+"F0.wireOp",EDGE,"E1.3")])],"isStart":false});
            extrude(context, id + "F3", {"entities" : qUnion([Q0]), "operationType" : NewBodyOperationType.ADD, "endBound" : BoundingType.UP_TO_SURFACE, "endBoundEntityFace" : qUnion([Q1]), "depth" : 4 * mm});
        }
        {
            var Q0;
            Q0=qCreatedBy(makeId("Top.planeOp"),FACE);
            var sketch = newSketch(context, id + "F4", { "sketchPlane" : qUnion([Q0])});
            skCircle(sketch, "E27.cCircle", {"center": v(-72, 41.57) * mm, "radius": 11.55 * mm, "construction": true});
            skLineSegment(sketch, "E27.0", {"start": v(-62, 35.8) * mm, "end": v(-72, 30.02) * mm});
            skLineSegment(sketch, "E27.4", {"start": v(-72, 53.12) * mm, "end": v(-62, 47.34) * mm});
            skLineSegment(sketch, "E27.5", {"start": v(-62, 47.34) * mm, "end": v(-62, 35.8) * mm});
            skCircle(sketch, "E28.cCircle", {"center": v(-72, -41.57) * mm, "radius": 11.55 * mm, "construction": true});
            skLineSegment(sketch, "E28.0", {"start": v(-62, -47.34) * mm, "end": v(-72, -53.12) * mm});
            skLineSegment(sketch, "E28.4", {"start": v(-72, -30.02) * mm, "end": v(-62, -35.8) * mm});
            skLineSegment(sketch, "E28.5", {"start": v(-62, -35.8) * mm, "end": v(-62, -47.34) * mm});
            skLineSegment(sketch, "E29.0", {"start": v(-70, -59) * mm, "end": v(-70, 59) * mm});
            skSolve(sketch);
        }
        {
            var Q0;
            Q0=qSketchRegion(id+"F4",true);
            var Q1;
            Q1=makeQuery(id+"F3.boolean.opBoolean","MERGE",FACE,{"derivedFrom":[makeQuery(id+"F1.opExtrude","CAP_FACE",FACE,{"disambiguationData":[OSD([sQuery(id+"F0.wireOp",EDGE,"E0.bottom"),sQuery(id+"F0.wireOp",EDGE,"E0.top"),sQuery(id+"F0.wireOp",EDGE,"E0.left"),sQuery(id+"F0.wireOp",EDGE,"E0.right"),sQuery(id+"F0.wireOp",EDGE,"E1.0"),sQuery(id+"F0.wireOp",EDGE,"E1.1"),sQuery(id+"F0.wireOp",EDGE,"E1.2"),sQuery(id+"F0.wireOp",EDGE,"E1.3")])],"isStart":false}),makeQuery(id+"F3.opExtrude","CAP_FACE",FACE,{"disambiguationData":[OSD([sQuery(id+"F2.wireOp",EDGE,"E2.0.1.1"),sQuery(id+"F2.wireOp",EDGE,"E2.0.1.5"),sQuery(id+"F2.wireOp",EDGE,"E2.0.1.13"),sQuery(id+"F2.wireOp",EDGE,"E2.0.2.1"),sQuery(id+"F2.wireOp",EDGE,"E2.0.2.5"),sQuery(id+"F2.wireOp",EDGE,"E2.0.2.13"),sQuery(id+"F2.wireOp",EDGE,"E2.0.3.1"),sQuery(id+"F2.wireOp",EDGE,"E2.0.3.5"),sQuery(id+"F2.wireOp",EDGE,"E2.0.3.13"),sQuery(id+"F2.wireOp",EDGE,"E2.1.0.7"),sQuery(id+"F2.wireOp",EDGE,"E2.1.0.8"),sQuery(id+"F2.wireOp",EDGE,"E2.1.1.1"),sQuery(id+"F2.wireOp",EDGE,"E2.1.1.2"),sQuery(id+"F2.wireOp",EDGE,"E2.1.1.3"),sQuery(id+"F2.wireOp",EDGE,"E2.1.1.4"),sQuery(id+"F2.wireOp",EDGE,"E2.1.1.5"),sQuery(id+"F2.wireOp",EDGE,"E2.1.1.6"),sQuery(id+"F2.wireOp",EDGE,"E2.1.1.7"),sQuery(id+"F2.wireOp",EDGE,"E2.1.1.8"),sQuery(id+"F2.wireOp",EDGE,"E2.1.1.10"),sQuery(id+"F2.wireOp",EDGE,"E2.1.1.11"),sQuery(id+"F2.wireOp",EDGE,"E2.1.1.13"),sQuery(id+"F2.wireOp",EDGE,"E2.1.2.1"),sQuery(id+"F2.wireOp",EDGE,"E2.1.2.2"),sQuery(id+"F2.wireOp",EDGE,"E2.1.2.3"),sQuery(id+"F2.wireOp",EDGE,"E2.1.2.4"),sQuery(id+"F2.wireOp",EDGE,"E2.1.2.5"),sQuery(id+"F2.wireOp",EDGE,"E2.1.2.6"),sQuery(id+"F2.wireOp",EDGE,"E2.1.2.7"),sQuery(id+"F2.wireOp",EDGE,"E2.1.2.8"),sQuery(id+"F2.wireOp",EDGE,"E2.1.2.10"),sQuery(id+"F2.wireOp",EDGE,"E2.1.2.11"),sQuery(id+"F2.wireOp",EDGE,"E2.1.2.13"),sQuery(id+"F2.wireOp",EDGE,"E2.1.3.1"),sQuery(id+"F2.wireOp",EDGE,"E2.1.3.2"),sQuery(id+"F2.wireOp",EDGE,"E2.1.3.3"),sQuery(id+"F2.wireOp",EDGE,"E2.1.3.4"),sQuery(id+"F2.wireOp",EDGE,"E2.1.3.5"),sQuery(id+"F2.wireOp",EDGE,"E2.1.3.10"),sQuery(id+"F2.wireOp",EDGE,"E2.1.3.11"),sQuery(id+"F2.wireOp",EDGE,"E2.1.3.13"),sQuery(id+"F2.wireOp",EDGE,"E2.2.0.7"),sQuery(id+"F2.wireOp",EDGE,"E2.2.0.8"),sQuery(id+"F2.wireOp",EDGE,"E2.2.1.1"),sQuery(id+"F2.wireOp",EDGE,"E2.2.1.2"),sQuery(id+"F2.wireOp",EDGE,"E2.2.1.3"),sQuery(id+"F2.wireOp",EDGE,"E2.2.1.4"),sQuery(id+"F2.wireOp",EDGE,"E2.2.1.5"),sQuery(id+"F2.wireOp",EDGE,"E2.2.1.6"),sQuery(id+"F2.wireOp",EDGE,"E2.2.1.7"),sQuery(id+"F2.wireOp",EDGE,"E2.2.1.8"),sQuery(id+"F2.wireOp",EDGE,"E2.2.1.9"),sQuery(id+"F2.wireOp",EDGE,"E2.2.1.10"),sQuery(id+"F2.wireOp",EDGE,"E2.2.1.11"),sQuery(id+"F2.wireOp",EDGE,"E2.2.1.13"),sQuery(id+"F2.wireOp",EDGE,"E2.2.2.1"),sQuery(id+"F2.wireOp",EDGE,"E2.2.2.2"),sQuery(id+"F2.wireOp",EDGE,"E2.2.2.3"),sQuery(id+"F2.wireOp",EDGE,"E2.2.2.4"),sQuery(id+"F2.wireOp",EDGE,"E2.2.2.5"),sQuery(id+"F2.wireOp",EDGE,"E2.2.2.6"),sQuery(id+"F2.wireOp",EDGE,"E2.2.2.7"),sQuery(id+"F2.wireOp",EDGE,"E2.2.2.8"),sQuery(id+"F2.wireOp",EDGE,"E2.2.2.9"),sQuery(id+"F2.wireOp",EDGE,"E2.2.2.10"),sQuery(id+"F2.wireOp",EDGE,"E2.2.2.11"),sQuery(id+"F2.wireOp",EDGE,"E2.2.2.13"),sQuery(id+"F2.wireOp",EDGE,"E2.2.3.1"),sQuery(id+"F2.wireOp",EDGE,"E2.2.3.2"),sQuery(id+"F2.wireOp",EDGE,"E2.2.3.3"),sQuery(id+"F2.wireOp",EDGE,"E2.2.3.4"),sQuery(id+"F2.wireOp",EDGE,"E2.2.3.5"),sQuery(id+"F2.wireOp",EDGE,"E2.2.3.10"),sQuery(id+"F2.wireOp",EDGE,"E2.2.3.11"),sQuery(id+"F2.wireOp",EDGE,"E2.2.3.13"),sQuery(id+"F2.wireOp",EDGE,"E2.3.0.7"),sQuery(id+"F2.wireOp",EDGE,"E2.3.0.8"),sQuery(id+"F2.wireOp",EDGE,"E2.3.1.1"),sQuery(id+"F2.wireOp",EDGE,"E2.3.1.2"),sQuery(id+"F2.wireOp",EDGE,"E2.3.1.3"),sQuery(id+"F2.wireOp",EDGE,"E2.3.1.4"),sQuery(id+"F2.wireOp",EDGE,"E2.3.1.5"),sQuery(id+"F2.wireOp",EDGE,"E2.3.1.6"),sQuery(id+"F2.wireOp",EDGE,"E2.3.1.7"),sQuery(id+"F2.wireOp",EDGE,"E2.3.1.8"),sQuery(id+"F2.wireOp",EDGE,"E2.3.1.9"),sQuery(id+"F2.wireOp",EDGE,"E2.3.1.10"),sQuery(id+"F2.wireOp",EDGE,"E2.3.1.11"),sQuery(id+"F2.wireOp",EDGE,"E2.3.1.13"),sQuery(id+"F2.wireOp",EDGE,"E2.3.2.1"),sQuery(id+"F2.wireOp",EDGE,"E2.3.2.2"),sQuery(id+"F2.wireOp",EDGE,"E2.3.2.3"),sQuery(id+"F2.wireOp",EDGE,"E2.3.2.4"),sQuery(id+"F2.wireOp",EDGE,"E2.3.2.5"),sQuery(id+"F2.wireOp",EDGE,"E2.3.2.6"),sQuery(id+"F2.wireOp",EDGE,"E2.3.2.7"),sQuery(id+"F2.wireOp",EDGE,"E2.3.2.8"),sQuery(id+"F2.wireOp",EDGE,"E2.3.2.9"),sQuery(id+"F2.wireOp",EDGE,"E2.3.2.10"),sQuery(id+"F2.wireOp",EDGE,"E2.3.2.11"),sQuery(id+"F2.wireOp",EDGE,"E2.3.2.13"),sQuery(id+"F2.wireOp",EDGE,"E2.3.3.1"),sQuery(id+"F2.wireOp",EDGE,"E2.3.3.2"),sQuery(id+"F2.wireOp",EDGE,"E2.3.3.3"),sQuery(id+"F2.wireOp",EDGE,"E2.3.3.4"),sQuery(id+"F2.wireOp",EDGE,"E2.3.3.5"),sQuery(id+"F2.wireOp",EDGE,"E2.3.3.10"),sQuery(id+"F2.wireOp",EDGE,"E2.3.3.11"),sQuery(id+"F2.wireOp",EDGE,"E2.3.3.13"),sQuery(id+"F2.wireOp",EDGE,"E2.4.0.7"),sQuery(id+"F2.wireOp",EDGE,"E2.4.0.8"),sQuery(id+"F2.wireOp",EDGE,"E2.4.1.1"),sQuery(id+"F2.wireOp",EDGE,"E2.4.1.2"),sQuery(id+"F2.wireOp",EDGE,"E2.4.1.3"),sQuery(id+"F2.wireOp",EDGE,"E2.4.1.4"),sQuery(id+"F2.wireOp",EDGE,"E2.4.1.5"),sQuery(id+"F2.wireOp",EDGE,"E2.4.1.6"),sQuery(id+"F2.wireOp",EDGE,"E2.4.1.7"),sQuery(id+"F2.wireOp",EDGE,"E2.4.1.8"),sQuery(id+"F2.wireOp",EDGE,"E2.4.1.9"),sQuery(id+"F2.wireOp",EDGE,"E2.4.1.10"),sQuery(id+"F2.wireOp",EDGE,"E2.4.1.11"),sQuery(id+"F2.wireOp",EDGE,"E2.4.1.13"),sQuery(id+"F2.wireOp",EDGE,"E2.4.2.1"),sQuery(id+"F2.wireOp",EDGE,"E2.4.2.2"),sQuery(id+"F2.wireOp",EDGE,"E2.4.2.3"),sQuery(id+"F2.wireOp",EDGE,"E2.4.2.4"),sQuery(id+"F2.wireOp",EDGE,"E2.4.2.5"),sQuery(id+"F2.wireOp",EDGE,"E2.4.2.6"),sQuery(id+"F2.wireOp",EDGE,"E2.4.2.7"),sQuery(id+"F2.wireOp",EDGE,"E2.4.2.8"),sQuery(id+"F2.wireOp",EDGE,"E2.4.2.9"),sQuery(id+"F2.wireOp",EDGE,"E2.4.2.10"),sQuery(id+"F2.wireOp",EDGE,"E2.4.2.11"),sQuery(id+"F2.wireOp",EDGE,"E2.4.2.13"),sQuery(id+"F2.wireOp",EDGE,"E2.4.3.1"),sQuery(id+"F2.wireOp",EDGE,"E2.4.3.2"),sQuery(id+"F2.wireOp",EDGE,"E2.4.3.3"),sQuery(id+"F2.wireOp",EDGE,"E2.4.3.4"),sQuery(id+"F2.wireOp",EDGE,"E2.4.3.5"),sQuery(id+"F2.wireOp",EDGE,"E2.4.3.10"),sQuery(id+"F2.wireOp",EDGE,"E2.4.3.11"),sQuery(id+"F2.wireOp",EDGE,"E2.4.3.13"),sQuery(id+"F2.wireOp",EDGE,"E2.5.0.7"),sQuery(id+"F2.wireOp",EDGE,"E2.5.0.8"),sQuery(id+"F2.wireOp",EDGE,"E2.5.1.1"),sQuery(id+"F2.wireOp",EDGE,"E2.5.1.2"),sQuery(id+"F2.wireOp",EDGE,"E2.5.1.3"),sQuery(id+"F2.wireOp",EDGE,"E2.5.1.4"),sQuery(id+"F2.wireOp",EDGE,"E2.5.1.5"),sQuery(id+"F2.wireOp",EDGE,"E2.5.1.6"),sQuery(id+"F2.wireOp",EDGE,"E2.5.1.7"),sQuery(id+"F2.wireOp",EDGE,"E2.5.1.8"),sQuery(id+"F2.wireOp",EDGE,"E2.5.1.9"),sQuery(id+"F2.wireOp",EDGE,"E2.5.1.10"),sQuery(id+"F2.wireOp",EDGE,"E2.5.1.11"),sQuery(id+"F2.wireOp",EDGE,"E2.5.1.13"),sQuery(id+"F2.wireOp",EDGE,"E2.5.2.1"),sQuery(id+"F2.wireOp",EDGE,"E2.5.2.2"),sQuery(id+"F2.wireOp",EDGE,"E2.5.2.3"),sQuery(id+"F2.wireOp",EDGE,"E2.5.2.4"),sQuery(id+"F2.wireOp",EDGE,"E2.5.2.5"),sQuery(id+"F2.wireOp",EDGE,"E2.5.2.6"),sQuery(id+"F2.wireOp",EDGE,"E2.5.2.7"),sQuery(id+"F2.wireOp",EDGE,"E2.5.2.8"),sQuery(id+"F2.wireOp",EDGE,"E2.5.2.9"),sQuery(id+"F2.wireOp",EDGE,"E2.5.2.10"),sQuery(id+"F2.wireOp",EDGE,"E2.5.2.11"),sQuery(id+"F2.wireOp",EDGE,"E2.5.2.13"),sQuery(id+"F2.wireOp",EDGE,"E2.5.3.1"),sQuery(id+"F2.wireOp",EDGE,"E2.5.3.2"),sQuery(id+"F2.wireOp",EDGE,"E2.5.3.3"),sQuery(id+"F2.wireOp",EDGE,"E2.5.3.4"),sQuery(id+"F2.wireOp",EDGE,"E2.5.3.5"),sQuery(id+"F2.wireOp",EDGE,"E2.5.3.10"),sQuery(id+"F2.wireOp",EDGE,"E2.5.3.11"),sQuery(id+"F2.wireOp",EDGE,"E2.5.3.13"),sQuery(id+"F2.wireOp",EDGE,"E2.6.0.7"),sQuery(id+"F2.wireOp",EDGE,"E2.6.0.8"),sQuery(id+"F2.wireOp",EDGE,"E2.6.1.2"),sQuery(id+"F2.wireOp",EDGE,"E2.6.1.3"),sQuery(id+"F2.wireOp",EDGE,"E2.6.1.4"),sQuery(id+"F2.wireOp",EDGE,"E2.6.1.7"),sQuery(id+"F2.wireOp",EDGE,"E2.6.1.8"),sQuery(id+"F2.wireOp",EDGE,"E2.6.1.9"),sQuery(id+"F2.wireOp",EDGE,"E2.6.1.10"),sQuery(id+"F2.wireOp",EDGE,"E2.6.1.11"),sQuery(id+"F2.wireOp",EDGE,"E2.6.2.2"),sQuery(id+"F2.wireOp",EDGE,"E2.6.2.3"),sQuery(id+"F2.wireOp",EDGE,"E2.6.2.4"),sQuery(id+"F2.wireOp",EDGE,"E2.6.2.7"),sQuery(id+"F2.wireOp",EDGE,"E2.6.2.8"),sQuery(id+"F2.wireOp",EDGE,"E2.6.2.9"),sQuery(id+"F2.wireOp",EDGE,"E2.6.2.10"),sQuery(id+"F2.wireOp",EDGE,"E2.6.2.11"),sQuery(id+"F2.wireOp",EDGE,"E2.6.3.2"),sQuery(id+"F2.wireOp",EDGE,"E2.6.3.3"),sQuery(id+"F2.wireOp",EDGE,"E2.6.3.4"),sQuery(id+"F2.wireOp",EDGE,"E2.6.3.10"),sQuery(id+"F2.wireOp",EDGE,"E2.6.3.11"),sQuery(id+"F2.wireOp",EDGE,"E3.0"),sQuery(id+"F2.wireOp",EDGE,"E3.1"),sQuery(id+"F2.wireOp",EDGE,"E3.2"),sQuery(id+"F2.wireOp",EDGE,"E3.3"),sQuery(id+"F2.wireOp",EDGE,"E4.trimOffspring"),sQuery(id+"F2.wireOp",EDGE,"E5.trimOffspring"),sQuery(id+"F2.wireOp",EDGE,"E6.trimOffspring"),sQuery(id+"F2.wireOp",EDGE,"E7.trimOffspring"),sQuery(id+"F2.wireOp",EDGE,"E8.trimOffspring"),sQuery(id+"F2.wireOp",EDGE,"E9.trimOffspring"),sQuery(id+"F2.wireOp",EDGE,"E10.trimOffspring"),sQuery(id+"F2.wireOp",EDGE,"E11.trimOffspring"),sQuery(id+"F2.wireOp",EDGE,"E12.trimOffspring"),sQuery(id+"F2.wireOp",EDGE,"E13.trimOffspring"),sQuery(id+"F2.wireOp",EDGE,"E14.trimOffspring"),sQuery(id+"F2.wireOp",EDGE,"E15.trimOffspring"),sQuery(id+"F2.wireOp",EDGE,"E16.trimOffspring"),sQuery(id+"F2.wireOp",EDGE,"E17.trimOffspring"),sQuery(id+"F2.wireOp",EDGE,"E18.trimOffspring"),sQuery(id+"F2.wireOp",EDGE,"E19.trimOffspring"),sQuery(id+"F2.wireOp",EDGE,"E20.trimOffspring"),sQuery(id+"F2.wireOp",EDGE,"E21.trimOffspring"),sQuery(id+"F2.wireOp",EDGE,"E22.trimOffspring"),sQuery(id+"F2.wireOp",EDGE,"E23.trimOffspring"),sQuery(id+"F2.wireOp",EDGE,"E24.trimOffspring"),sQuery(id+"F2.wireOp",EDGE,"E25.trimOffspring"),sQuery(id+"F2.wireOp",EDGE,"E26.0"),sQuery(id+"F2.wireOp",EDGE,"E26.1"),sQuery(id+"F2.wireOp",EDGE,"E26.2"),sQuery(id+"F2.wireOp",EDGE,"E26.3")])],"isStart":false})]});
            extrude(context, id + "F5", {"entities" : qUnion([Q0]), "operationType" : NewBodyOperationType.ADD, "endBound" : BoundingType.UP_TO_SURFACE, "endBoundEntityFace" : qUnion([Q1]), "depth" : 25 * mm});
        }
        {
            var Q0;
            Q0=qCreatedBy(makeId("Top.planeOp"),FACE);
            var sketch = newSketch(context, id + "F6", { "sketchPlane" : qUnion([Q0])});
            skCircle(sketch, "E30.cCircle", {"center": v(-68, 0) * mm, "radius": 11.55 * mm, "construction": true});
            skLineSegment(sketch, "E30.1", {"start": v(-70, -10.4) * mm, "end": v(-78, -5.77) * mm, "construction": true});
            skLineSegment(sketch, "E30.2", {"start": v(-78, -5.77) * mm, "end": v(-78, 5.77) * mm, "construction": true});
            skLineSegment(sketch, "E30.3", {"start": v(-78, 5.77) * mm, "end": v(-70, 10.4) * mm, "construction": true});
            skLineSegment(sketch, "E30.5", {"start": v(-58, 5.77) * mm, "end": v(-58, -5.77) * mm});
            skLineSegment(sketch, "E31.0", {"start": v(-70, -31.18) * mm, "end": v(-70, 31.18) * mm});
            skPoint(sketch, "E32.orphan", {"position": v(-68, -11.55) * mm});
            skLineSegment(sketch, "E33.0", {"start": v(-74.5, 3.75) * mm, "end": v(-68.25, 7.36) * mm});
            skLineSegment(sketch, "E33.1", {"start": v(-74.5, -3.75) * mm, "end": v(-74.5, 3.75) * mm});
            skLineSegment(sketch, "E33.2", {"start": v(-68.25, -7.36) * mm, "end": v(-74.5, -3.75) * mm});
            skCircle(sketch, "E34.cCircle", {"center": v(36, 57.74) * mm, "radius": 11.55 * mm, "construction": true});
            skLineSegment(sketch, "E34.0", {"start": v(46, 63.5) * mm, "end": v(46, 51.96) * mm, "construction": true});
            skLineSegment(sketch, "E34.1", {"start": v(46, 51.96) * mm, "end": v(36, 46.19) * mm, "construction": true});
            skLineSegment(sketch, "E34.2", {"start": v(36, 46.19) * mm, "end": v(26, 51.96) * mm, "construction": true});
            skLineSegment(sketch, "E34.3", {"start": v(26, 51.96) * mm, "end": v(26, 63.5) * mm, "construction": true});
            skLineSegment(sketch, "E34.4", {"start": v(26, 63.5) * mm, "end": v(36, 69.28) * mm, "construction": true});
            skLineSegment(sketch, "E34.5", {"start": v(36, 69.28) * mm, "end": v(46, 63.5) * mm, "construction": true});
            skCircle(sketch, "E35.cCircle", {"center": v(-36, 57.74) * mm, "radius": 11.55 * mm, "construction": true});
            skLineSegment(sketch, "E35.0", {"start": v(-36, 46.19) * mm, "end": v(-46, 51.96) * mm, "construction": true});
            skLineSegment(sketch, "E35.1", {"start": v(-46, 51.96) * mm, "end": v(-46, 63.5) * mm, "construction": true});
            skLineSegment(sketch, "E35.2", {"start": v(-46, 63.5) * mm, "end": v(-36, 69.28) * mm, "construction": true});
            skLineSegment(sketch, "E35.3", {"start": v(-36, 69.28) * mm, "end": v(-26, 63.5) * mm, "construction": true});
            skLineSegment(sketch, "E35.4", {"start": v(-26, 63.5) * mm, "end": v(-26, 51.96) * mm, "construction": true});
            skLineSegment(sketch, "E35.5", {"start": v(-26, 51.96) * mm, "end": v(-36, 46.19) * mm, "construction": true});
            skCircle(sketch, "E36.cCircle", {"center": v(-36, -57.74) * mm, "radius": 11.55 * mm, "construction": true});
            skLineSegment(sketch, "E36.0", {"start": v(-26, -63.5) * mm, "end": v(-36, -69.28) * mm, "construction": true});
            skLineSegment(sketch, "E36.1", {"start": v(-36, -69.28) * mm, "end": v(-46, -63.5) * mm, "construction": true});
            skLineSegment(sketch, "E36.2", {"start": v(-46, -63.5) * mm, "end": v(-46, -51.96) * mm, "construction": true});
            skLineSegment(sketch, "E36.3", {"start": v(-46, -51.96) * mm, "end": v(-36, -46.19) * mm, "construction": true});
            skLineSegment(sketch, "E36.4", {"start": v(-36, -46.19) * mm, "end": v(-26, -51.96) * mm, "construction": true});
            skLineSegment(sketch, "E36.5", {"start": v(-26, -51.96) * mm, "end": v(-26, -63.5) * mm, "construction": true});
            skCircle(sketch, "E37.cCircle", {"center": v(36, -57.74) * mm, "radius": 11.55 * mm, "construction": true});
            skLineSegment(sketch, "E37.0", {"start": v(46, -63.5) * mm, "end": v(36, -69.28) * mm, "construction": true});
            skLineSegment(sketch, "E37.1", {"start": v(36, -69.28) * mm, "end": v(26, -63.5) * mm, "construction": true});
            skLineSegment(sketch, "E37.2", {"start": v(26, -63.5) * mm, "end": v(26, -51.96) * mm, "construction": true});
            skLineSegment(sketch, "E37.3", {"start": v(26, -51.96) * mm, "end": v(36, -46.19) * mm, "construction": true});
            skLineSegment(sketch, "E37.4", {"start": v(36, -46.19) * mm, "end": v(46, -51.96) * mm, "construction": true});
            skLineSegment(sketch, "E37.5", {"start": v(46, -51.96) * mm, "end": v(46, -63.5) * mm, "construction": true});
            skLineSegment(sketch, "E38.0", {"start": v(70, 59) * mm, "end": v(-70, 59) * mm});
            skLineSegment(sketch, "E39.0", {"start": v(-45.5, 51.96) * mm, "end": v(-45.5, 63.5) * mm});
            skLineSegment(sketch, "E40.0", {"start": v(-26.5, 63.5) * mm, "end": v(-26.5, 51.96) * mm});
            skLineSegment(sketch, "E41.0", {"start": v(26.5, 51.96) * mm, "end": v(26.5, 63.5) * mm});
            skLineSegment(sketch, "E42.0", {"start": v(45.5, 63.5) * mm, "end": v(45.5, 51.96) * mm});
            skLineSegment(sketch, "E43.0", {"start": v(-45.5, -63.5) * mm, "end": v(-45.5, -51.96) * mm});
            skLineSegment(sketch, "E44.0", {"start": v(-26.5, -51.96) * mm, "end": v(-26.5, -63.5) * mm});
            skLineSegment(sketch, "E45.0", {"start": v(26.5, -63.5) * mm, "end": v(26.5, -51.96) * mm});
            skLineSegment(sketch, "E46.0", {"start": v(45.5, -51.96) * mm, "end": v(45.5, -63.5) * mm});
            skLineSegment(sketch, "E47.0", {"start": v(-36, 66.63) * mm, "end": v(-24.7, 60.1) * mm});
            skLineSegment(sketch, "E47.1", {"start": v(-47.3, 60.1) * mm, "end": v(-36, 66.63) * mm});
            skLineSegment(sketch, "E48.0", {"start": v(36, 66.63) * mm, "end": v(47.3, 60.1) * mm});
            skLineSegment(sketch, "E48.1", {"start": v(24.7, 60.1) * mm, "end": v(36, 66.63) * mm});
            skLineSegment(sketch, "E49.0", {"start": v(-36, -66.63) * mm, "end": v(-47.3, -60.1) * mm});
            skLineSegment(sketch, "E49.1", {"start": v(-24.7, -60.1) * mm, "end": v(-36, -66.63) * mm});
            skLineSegment(sketch, "E50.0", {"start": v(36, -66.63) * mm, "end": v(24.7, -60.1) * mm});
            skLineSegment(sketch, "E50.1", {"start": v(47.3, -60.1) * mm, "end": v(36, -66.63) * mm});
            skLineSegment(sketch, "E51.0", {"start": v(70, -59) * mm, "end": v(-70, -59) * mm});
            skSolve(sketch);
        }
        {
            var Q0;
            Q0=qSketchRegion(id+"F6",true);
            var Q1;
            Q1=makeQuery(id+"F3.boolean.opBoolean","MERGE",FACE,{"derivedFrom":[makeQuery(id+"F1.opExtrude","CAP_FACE",FACE,{"disambiguationData":[OSD([sQuery(id+"F0.wireOp",EDGE,"E0.bottom"),sQuery(id+"F0.wireOp",EDGE,"E0.top"),sQuery(id+"F0.wireOp",EDGE,"E0.left"),sQuery(id+"F0.wireOp",EDGE,"E0.right"),sQuery(id+"F0.wireOp",EDGE,"E1.0"),sQuery(id+"F0.wireOp",EDGE,"E1.1"),sQuery(id+"F0.wireOp",EDGE,"E1.2"),sQuery(id+"F0.wireOp",EDGE,"E1.3")])],"isStart":false}),makeQuery(id+"F3.opExtrude","CAP_FACE",FACE,{"disambiguationData":[OSD([sQuery(id+"F2.wireOp",EDGE,"E2.0.1.1"),sQuery(id+"F2.wireOp",EDGE,"E2.0.1.5"),sQuery(id+"F2.wireOp",EDGE,"E2.0.1.13"),sQuery(id+"F2.wireOp",EDGE,"E2.0.2.1"),sQuery(id+"F2.wireOp",EDGE,"E2.0.2.5"),sQuery(id+"F2.wireOp",EDGE,"E2.0.2.13"),sQuery(id+"F2.wireOp",EDGE,"E2.0.3.1"),sQuery(id+"F2.wireOp",EDGE,"E2.0.3.5"),sQuery(id+"F2.wireOp",EDGE,"E2.0.3.13"),sQuery(id+"F2.wireOp",EDGE,"E2.1.0.7"),sQuery(id+"F2.wireOp",EDGE,"E2.1.0.8"),sQuery(id+"F2.wireOp",EDGE,"E2.1.1.1"),sQuery(id+"F2.wireOp",EDGE,"E2.1.1.2"),sQuery(id+"F2.wireOp",EDGE,"E2.1.1.3"),sQuery(id+"F2.wireOp",EDGE,"E2.1.1.4"),sQuery(id+"F2.wireOp",EDGE,"E2.1.1.5"),sQuery(id+"F2.wireOp",EDGE,"E2.1.1.6"),sQuery(id+"F2.wireOp",EDGE,"E2.1.1.7"),sQuery(id+"F2.wireOp",EDGE,"E2.1.1.8"),sQuery(id+"F2.wireOp",EDGE,"E2.1.1.10"),sQuery(id+"F2.wireOp",EDGE,"E2.1.1.11"),sQuery(id+"F2.wireOp",EDGE,"E2.1.1.13"),sQuery(id+"F2.wireOp",EDGE,"E2.1.2.1"),sQuery(id+"F2.wireOp",EDGE,"E2.1.2.2"),sQuery(id+"F2.wireOp",EDGE,"E2.1.2.3"),sQuery(id+"F2.wireOp",EDGE,"E2.1.2.4"),sQuery(id+"F2.wireOp",EDGE,"E2.1.2.5"),sQuery(id+"F2.wireOp",EDGE,"E2.1.2.6"),sQuery(id+"F2.wireOp",EDGE,"E2.1.2.7"),sQuery(id+"F2.wireOp",EDGE,"E2.1.2.8"),sQuery(id+"F2.wireOp",EDGE,"E2.1.2.10"),sQuery(id+"F2.wireOp",EDGE,"E2.1.2.11"),sQuery(id+"F2.wireOp",EDGE,"E2.1.2.13"),sQuery(id+"F2.wireOp",EDGE,"E2.1.3.1"),sQuery(id+"F2.wireOp",EDGE,"E2.1.3.2"),sQuery(id+"F2.wireOp",EDGE,"E2.1.3.3"),sQuery(id+"F2.wireOp",EDGE,"E2.1.3.4"),sQuery(id+"F2.wireOp",EDGE,"E2.1.3.5"),sQuery(id+"F2.wireOp",EDGE,"E2.1.3.10"),sQuery(id+"F2.wireOp",EDGE,"E2.1.3.11"),sQuery(id+"F2.wireOp",EDGE,"E2.1.3.13"),sQuery(id+"F2.wireOp",EDGE,"E2.2.0.7"),sQuery(id+"F2.wireOp",EDGE,"E2.2.0.8"),sQuery(id+"F2.wireOp",EDGE,"E2.2.1.1"),sQuery(id+"F2.wireOp",EDGE,"E2.2.1.2"),sQuery(id+"F2.wireOp",EDGE,"E2.2.1.3"),sQuery(id+"F2.wireOp",EDGE,"E2.2.1.4"),sQuery(id+"F2.wireOp",EDGE,"E2.2.1.5"),sQuery(id+"F2.wireOp",EDGE,"E2.2.1.6"),sQuery(id+"F2.wireOp",EDGE,"E2.2.1.7"),sQuery(id+"F2.wireOp",EDGE,"E2.2.1.8"),sQuery(id+"F2.wireOp",EDGE,"E2.2.1.9"),sQuery(id+"F2.wireOp",EDGE,"E2.2.1.10"),sQuery(id+"F2.wireOp",EDGE,"E2.2.1.11"),sQuery(id+"F2.wireOp",EDGE,"E2.2.1.13"),sQuery(id+"F2.wireOp",EDGE,"E2.2.2.1"),sQuery(id+"F2.wireOp",EDGE,"E2.2.2.2"),sQuery(id+"F2.wireOp",EDGE,"E2.2.2.3"),sQuery(id+"F2.wireOp",EDGE,"E2.2.2.4"),sQuery(id+"F2.wireOp",EDGE,"E2.2.2.5"),sQuery(id+"F2.wireOp",EDGE,"E2.2.2.6"),sQuery(id+"F2.wireOp",EDGE,"E2.2.2.7"),sQuery(id+"F2.wireOp",EDGE,"E2.2.2.8"),sQuery(id+"F2.wireOp",EDGE,"E2.2.2.9"),sQuery(id+"F2.wireOp",EDGE,"E2.2.2.10"),sQuery(id+"F2.wireOp",EDGE,"E2.2.2.11"),sQuery(id+"F2.wireOp",EDGE,"E2.2.2.13"),sQuery(id+"F2.wireOp",EDGE,"E2.2.3.1"),sQuery(id+"F2.wireOp",EDGE,"E2.2.3.2"),sQuery(id+"F2.wireOp",EDGE,"E2.2.3.3"),sQuery(id+"F2.wireOp",EDGE,"E2.2.3.4"),sQuery(id+"F2.wireOp",EDGE,"E2.2.3.5"),sQuery(id+"F2.wireOp",EDGE,"E2.2.3.10"),sQuery(id+"F2.wireOp",EDGE,"E2.2.3.11"),sQuery(id+"F2.wireOp",EDGE,"E2.2.3.13"),sQuery(id+"F2.wireOp",EDGE,"E2.3.0.7"),sQuery(id+"F2.wireOp",EDGE,"E2.3.0.8"),sQuery(id+"F2.wireOp",EDGE,"E2.3.1.1"),sQuery(id+"F2.wireOp",EDGE,"E2.3.1.2"),sQuery(id+"F2.wireOp",EDGE,"E2.3.1.3"),sQuery(id+"F2.wireOp",EDGE,"E2.3.1.4"),sQuery(id+"F2.wireOp",EDGE,"E2.3.1.5"),sQuery(id+"F2.wireOp",EDGE,"E2.3.1.6"),sQuery(id+"F2.wireOp",EDGE,"E2.3.1.7"),sQuery(id+"F2.wireOp",EDGE,"E2.3.1.8"),sQuery(id+"F2.wireOp",EDGE,"E2.3.1.9"),sQuery(id+"F2.wireOp",EDGE,"E2.3.1.10"),sQuery(id+"F2.wireOp",EDGE,"E2.3.1.11"),sQuery(id+"F2.wireOp",EDGE,"E2.3.1.13"),sQuery(id+"F2.wireOp",EDGE,"E2.3.2.1"),sQuery(id+"F2.wireOp",EDGE,"E2.3.2.2"),sQuery(id+"F2.wireOp",EDGE,"E2.3.2.3"),sQuery(id+"F2.wireOp",EDGE,"E2.3.2.4"),sQuery(id+"F2.wireOp",EDGE,"E2.3.2.5"),sQuery(id+"F2.wireOp",EDGE,"E2.3.2.6"),sQuery(id+"F2.wireOp",EDGE,"E2.3.2.7"),sQuery(id+"F2.wireOp",EDGE,"E2.3.2.8"),sQuery(id+"F2.wireOp",EDGE,"E2.3.2.9"),sQuery(id+"F2.wireOp",EDGE,"E2.3.2.10"),sQuery(id+"F2.wireOp",EDGE,"E2.3.2.11"),sQuery(id+"F2.wireOp",EDGE,"E2.3.2.13"),sQuery(id+"F2.wireOp",EDGE,"E2.3.3.1"),sQuery(id+"F2.wireOp",EDGE,"E2.3.3.2"),sQuery(id+"F2.wireOp",EDGE,"E2.3.3.3"),sQuery(id+"F2.wireOp",EDGE,"E2.3.3.4"),sQuery(id+"F2.wireOp",EDGE,"E2.3.3.5"),sQuery(id+"F2.wireOp",EDGE,"E2.3.3.10"),sQuery(id+"F2.wireOp",EDGE,"E2.3.3.11"),sQuery(id+"F2.wireOp",EDGE,"E2.3.3.13"),sQuery(id+"F2.wireOp",EDGE,"E2.4.0.7"),sQuery(id+"F2.wireOp",EDGE,"E2.4.0.8"),sQuery(id+"F2.wireOp",EDGE,"E2.4.1.1"),sQuery(id+"F2.wireOp",EDGE,"E2.4.1.2"),sQuery(id+"F2.wireOp",EDGE,"E2.4.1.3"),sQuery(id+"F2.wireOp",EDGE,"E2.4.1.4"),sQuery(id+"F2.wireOp",EDGE,"E2.4.1.5"),sQuery(id+"F2.wireOp",EDGE,"E2.4.1.6"),sQuery(id+"F2.wireOp",EDGE,"E2.4.1.7"),sQuery(id+"F2.wireOp",EDGE,"E2.4.1.8"),sQuery(id+"F2.wireOp",EDGE,"E2.4.1.9"),sQuery(id+"F2.wireOp",EDGE,"E2.4.1.10"),sQuery(id+"F2.wireOp",EDGE,"E2.4.1.11"),sQuery(id+"F2.wireOp",EDGE,"E2.4.1.13"),sQuery(id+"F2.wireOp",EDGE,"E2.4.2.1"),sQuery(id+"F2.wireOp",EDGE,"E2.4.2.2"),sQuery(id+"F2.wireOp",EDGE,"E2.4.2.3"),sQuery(id+"F2.wireOp",EDGE,"E2.4.2.4"),sQuery(id+"F2.wireOp",EDGE,"E2.4.2.5"),sQuery(id+"F2.wireOp",EDGE,"E2.4.2.6"),sQuery(id+"F2.wireOp",EDGE,"E2.4.2.7"),sQuery(id+"F2.wireOp",EDGE,"E2.4.2.8"),sQuery(id+"F2.wireOp",EDGE,"E2.4.2.9"),sQuery(id+"F2.wireOp",EDGE,"E2.4.2.10"),sQuery(id+"F2.wireOp",EDGE,"E2.4.2.11"),sQuery(id+"F2.wireOp",EDGE,"E2.4.2.13"),sQuery(id+"F2.wireOp",EDGE,"E2.4.3.1"),sQuery(id+"F2.wireOp",EDGE,"E2.4.3.2"),sQuery(id+"F2.wireOp",EDGE,"E2.4.3.3"),sQuery(id+"F2.wireOp",EDGE,"E2.4.3.4"),sQuery(id+"F2.wireOp",EDGE,"E2.4.3.5"),sQuery(id+"F2.wireOp",EDGE,"E2.4.3.10"),sQuery(id+"F2.wireOp",EDGE,"E2.4.3.11"),sQuery(id+"F2.wireOp",EDGE,"E2.4.3.13"),sQuery(id+"F2.wireOp",EDGE,"E2.5.0.7"),sQuery(id+"F2.wireOp",EDGE,"E2.5.0.8"),sQuery(id+"F2.wireOp",EDGE,"E2.5.1.1"),sQuery(id+"F2.wireOp",EDGE,"E2.5.1.2"),sQuery(id+"F2.wireOp",EDGE,"E2.5.1.3"),sQuery(id+"F2.wireOp",EDGE,"E2.5.1.4"),sQuery(id+"F2.wireOp",EDGE,"E2.5.1.5"),sQuery(id+"F2.wireOp",EDGE,"E2.5.1.6"),sQuery(id+"F2.wireOp",EDGE,"E2.5.1.7"),sQuery(id+"F2.wireOp",EDGE,"E2.5.1.8"),sQuery(id+"F2.wireOp",EDGE,"E2.5.1.9"),sQuery(id+"F2.wireOp",EDGE,"E2.5.1.10"),sQuery(id+"F2.wireOp",EDGE,"E2.5.1.11"),sQuery(id+"F2.wireOp",EDGE,"E2.5.1.13"),sQuery(id+"F2.wireOp",EDGE,"E2.5.2.1"),sQuery(id+"F2.wireOp",EDGE,"E2.5.2.2"),sQuery(id+"F2.wireOp",EDGE,"E2.5.2.3"),sQuery(id+"F2.wireOp",EDGE,"E2.5.2.4"),sQuery(id+"F2.wireOp",EDGE,"E2.5.2.5"),sQuery(id+"F2.wireOp",EDGE,"E2.5.2.6"),sQuery(id+"F2.wireOp",EDGE,"E2.5.2.7"),sQuery(id+"F2.wireOp",EDGE,"E2.5.2.8"),sQuery(id+"F2.wireOp",EDGE,"E2.5.2.9"),sQuery(id+"F2.wireOp",EDGE,"E2.5.2.10"),sQuery(id+"F2.wireOp",EDGE,"E2.5.2.11"),sQuery(id+"F2.wireOp",EDGE,"E2.5.2.13"),sQuery(id+"F2.wireOp",EDGE,"E2.5.3.1"),sQuery(id+"F2.wireOp",EDGE,"E2.5.3.2"),sQuery(id+"F2.wireOp",EDGE,"E2.5.3.3"),sQuery(id+"F2.wireOp",EDGE,"E2.5.3.4"),sQuery(id+"F2.wireOp",EDGE,"E2.5.3.5"),sQuery(id+"F2.wireOp",EDGE,"E2.5.3.10"),sQuery(id+"F2.wireOp",EDGE,"E2.5.3.11"),sQuery(id+"F2.wireOp",EDGE,"E2.5.3.13"),sQuery(id+"F2.wireOp",EDGE,"E2.6.0.7"),sQuery(id+"F2.wireOp",EDGE,"E2.6.0.8"),sQuery(id+"F2.wireOp",EDGE,"E2.6.1.2"),sQuery(id+"F2.wireOp",EDGE,"E2.6.1.3"),sQuery(id+"F2.wireOp",EDGE,"E2.6.1.4"),sQuery(id+"F2.wireOp",EDGE,"E2.6.1.7"),sQuery(id+"F2.wireOp",EDGE,"E2.6.1.8"),sQuery(id+"F2.wireOp",EDGE,"E2.6.1.9"),sQuery(id+"F2.wireOp",EDGE,"E2.6.1.10"),sQuery(id+"F2.wireOp",EDGE,"E2.6.1.11"),sQuery(id+"F2.wireOp",EDGE,"E2.6.2.2"),sQuery(id+"F2.wireOp",EDGE,"E2.6.2.3"),sQuery(id+"F2.wireOp",EDGE,"E2.6.2.4"),sQuery(id+"F2.wireOp",EDGE,"E2.6.2.7"),sQuery(id+"F2.wireOp",EDGE,"E2.6.2.8"),sQuery(id+"F2.wireOp",EDGE,"E2.6.2.9"),sQuery(id+"F2.wireOp",EDGE,"E2.6.2.10"),sQuery(id+"F2.wireOp",EDGE,"E2.6.2.11"),sQuery(id+"F2.wireOp",EDGE,"E2.6.3.2"),sQuery(id+"F2.wireOp",EDGE,"E2.6.3.3"),sQuery(id+"F2.wireOp",EDGE,"E2.6.3.4"),sQuery(id+"F2.wireOp",EDGE,"E2.6.3.10"),sQuery(id+"F2.wireOp",EDGE,"E2.6.3.11"),sQuery(id+"F2.wireOp",EDGE,"E3.0"),sQuery(id+"F2.wireOp",EDGE,"E3.1"),sQuery(id+"F2.wireOp",EDGE,"E3.2"),sQuery(id+"F2.wireOp",EDGE,"E3.3"),sQuery(id+"F2.wireOp",EDGE,"E4.trimOffspring"),sQuery(id+"F2.wireOp",EDGE,"E5.trimOffspring"),sQuery(id+"F2.wireOp",EDGE,"E6.trimOffspring"),sQuery(id+"F2.wireOp",EDGE,"E7.trimOffspring"),sQuery(id+"F2.wireOp",EDGE,"E8.trimOffspring"),sQuery(id+"F2.wireOp",EDGE,"E9.trimOffspring"),sQuery(id+"F2.wireOp",EDGE,"E10.trimOffspring"),sQuery(id+"F2.wireOp",EDGE,"E11.trimOffspring"),sQuery(id+"F2.wireOp",EDGE,"E12.trimOffspring"),sQuery(id+"F2.wireOp",EDGE,"E13.trimOffspring"),sQuery(id+"F2.wireOp",EDGE,"E14.trimOffspring"),sQuery(id+"F2.wireOp",EDGE,"E15.trimOffspring"),sQuery(id+"F2.wireOp",EDGE,"E16.trimOffspring"),sQuery(id+"F2.wireOp",EDGE,"E17.trimOffspring"),sQuery(id+"F2.wireOp",EDGE,"E18.trimOffspring"),sQuery(id+"F2.wireOp",EDGE,"E19.trimOffspring"),sQuery(id+"F2.wireOp",EDGE,"E20.trimOffspring"),sQuery(id+"F2.wireOp",EDGE,"E21.trimOffspring"),sQuery(id+"F2.wireOp",EDGE,"E22.trimOffspring"),sQuery(id+"F2.wireOp",EDGE,"E23.trimOffspring"),sQuery(id+"F2.wireOp",EDGE,"E24.trimOffspring"),sQuery(id+"F2.wireOp",EDGE,"E25.trimOffspring"),sQuery(id+"F2.wireOp",EDGE,"E26.0"),sQuery(id+"F2.wireOp",EDGE,"E26.1"),sQuery(id+"F2.wireOp",EDGE,"E26.2"),sQuery(id+"F2.wireOp",EDGE,"E26.3")])],"isStart":false})]});
            extrude(context, id + "F7", {"entities" : qUnion([Q0]), "operationType" : NewBodyOperationType.ADD, "endBound" : BoundingType.UP_TO_SURFACE, "endBoundEntityFace" : qUnion([Q1]), "depth" : 4 * mm});
        }
        {
            var Q0;
            Q0=qCreatedBy(makeId("Top.planeOp"),FACE);
            var sketch = newSketch(context, id + "F8", { "sketchPlane" : qUnion([Q0])});
            skLineSegment(sketch, "E52.0", {"start": v(-66, 49.65) * mm, "end": v(-62, 47.34) * mm, "construction": true});
            skLineSegment(sketch, "E52.1", {"start": v(-62, 47.34) * mm, "end": v(-62, 35.8) * mm, "construction": true});
            skLineSegment(sketch, "E52.2", {"start": v(-62, 35.8) * mm, "end": v(-66, 33.49) * mm, "construction": true});
            skLineSegment(sketch, "E52.3", {"start": v(-66, -33.49) * mm, "end": v(-62, -35.8) * mm, "construction": true});
            skLineSegment(sketch, "E52.4", {"start": v(-62, -35.8) * mm, "end": v(-62, -47.34) * mm, "construction": true});
            skLineSegment(sketch, "E52.5", {"start": v(-62, -47.34) * mm, "end": v(-66, -49.65) * mm, "construction": true});
            skCircle(sketch, "E53.cCircle", {"center": v(-72, 41.57) * mm, "radius": 11.55 * mm, "construction": true});
            skLineSegment(sketch, "E53.0", {"start": v(-72, 30.02) * mm, "end": v(-82, 35.8) * mm, "construction": true});
            skLineSegment(sketch, "E53.1", {"start": v(-82, 35.8) * mm, "end": v(-82, 47.34) * mm, "construction": true});
            skLineSegment(sketch, "E53.2", {"start": v(-82, 47.34) * mm, "end": v(-72, 53.12) * mm, "construction": true});
            skLineSegment(sketch, "E53.3", {"start": v(-72, 53.12) * mm, "end": v(-62, 47.34) * mm, "construction": true});
            skLineSegment(sketch, "E53.5", {"start": v(-62, 35.8) * mm, "end": v(-72, 30.02) * mm, "construction": true});
            skCircle(sketch, "E54.cCircle", {"center": v(-72, -41.57) * mm, "radius": 11.55 * mm, "construction": true});
            skLineSegment(sketch, "E54.0", {"start": v(-62, -47.34) * mm, "end": v(-72, -53.12) * mm, "construction": true});
            skLineSegment(sketch, "E54.1", {"start": v(-72, -53.12) * mm, "end": v(-82, -47.34) * mm, "construction": true});
            skLineSegment(sketch, "E54.2", {"start": v(-82, -47.34) * mm, "end": v(-82, -35.8) * mm, "construction": true});
            skLineSegment(sketch, "E54.3", {"start": v(-82, -35.8) * mm, "end": v(-72, -30.02) * mm, "construction": true});
            skLineSegment(sketch, "E54.4", {"start": v(-72, -30.02) * mm, "end": v(-62, -35.8) * mm, "construction": true});
            skLineSegment(sketch, "E55.0", {"start": v(-65, 37.53) * mm, "end": v(-73.5, 32.62) * mm});
            skLineSegment(sketch, "E55.1", {"start": v(-65, 45.61) * mm, "end": v(-65, 37.53) * mm});
            skLineSegment(sketch, "E55.2", {"start": v(-73.5, 50.52) * mm, "end": v(-65, 45.61) * mm});
            skLineSegment(sketch, "E56.0", {"start": v(-65, -45.61) * mm, "end": v(-73.5, -50.52) * mm});
            skLineSegment(sketch, "E56.1", {"start": v(-65, -37.53) * mm, "end": v(-65, -45.61) * mm});
            skLineSegment(sketch, "E56.2", {"start": v(-73.5, -32.62) * mm, "end": v(-65, -37.53) * mm});
            skLineSegment(sketch, "E57.0", {"start": v(-70, 6.35) * mm, "end": v(-70, 59) * mm});
            skLineSegment(sketch, "E58.0", {"start": v(-70, -59) * mm, "end": v(-70, -6.35) * mm});
            skSolve(sketch);
        }
        {
            var Q0;
            Q0 = qSketchRegion(id + "F8", true);
            extrude(context, id + "F9", {"entities" : qUnion([Q0]), "operationType" : NewBodyOperationType.REMOVE, "endBound" : BoundingType.THROUGH_ALL, "depth" : 25 * mm});
        }
    });
